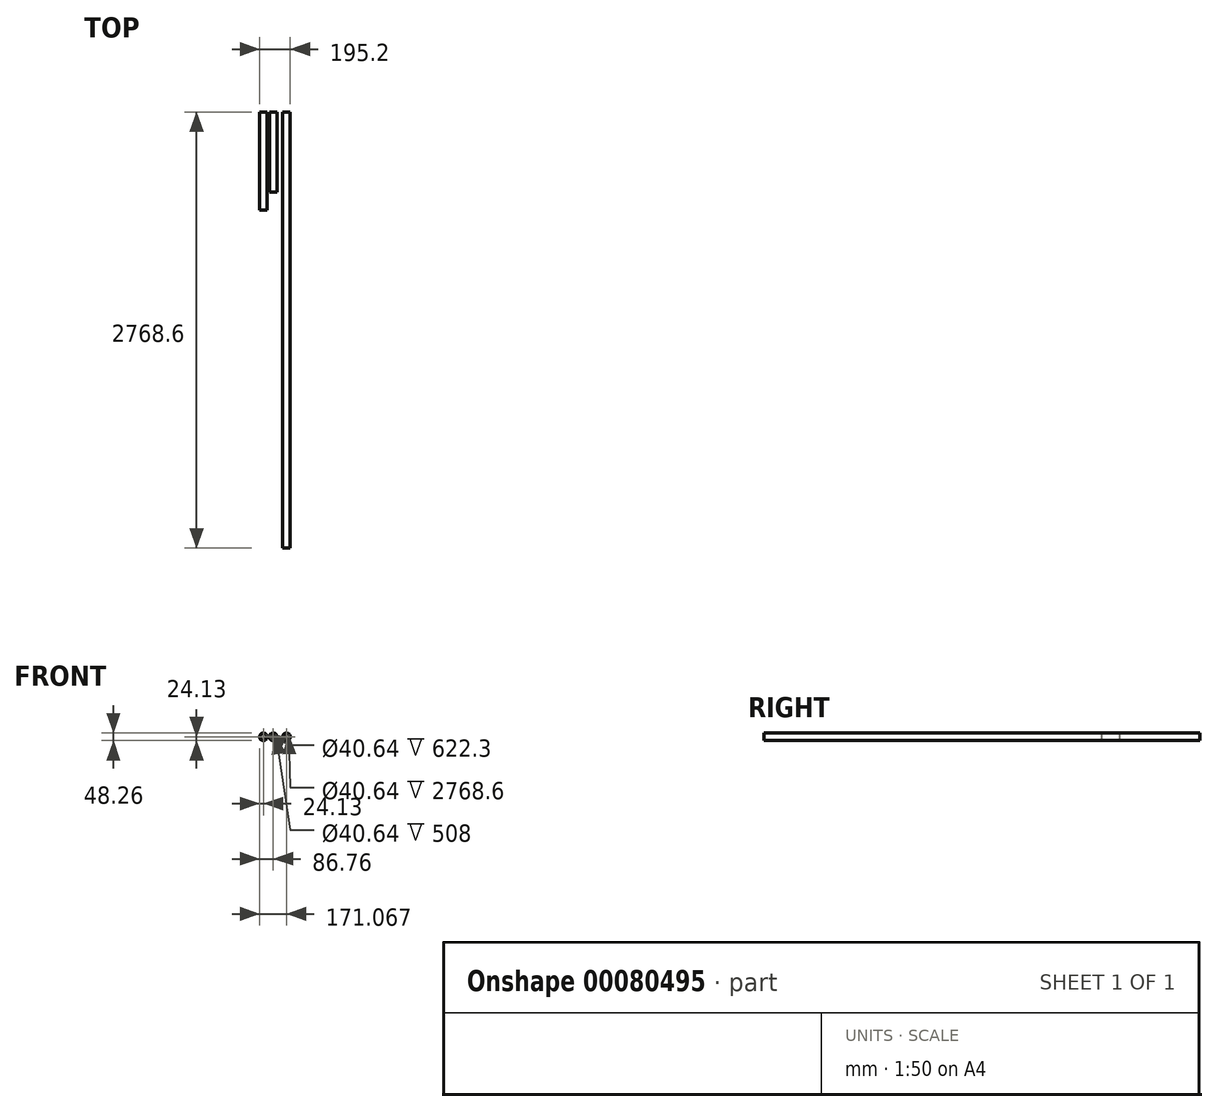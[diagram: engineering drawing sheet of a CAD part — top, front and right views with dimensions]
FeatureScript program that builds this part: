
annotation { "Feature Type Name" : "Feature", "Feature Type Description" : "" }
export const myFeature = defineFeature(function(context is Context, id is Id, definition is map)
    precondition{}
    {
        {
            var Q0;
            Q0=qCreatedBy(makeId("Front.planeOp"),FACE);
            var sketch = newSketch(context, id + "F0", { "sketchPlane" : qUnion([Q0])});
            skCircle(sketch, "E0", {"center": v(0, 0) * mm, "radius": 20.32 * mm});
            skCircle(sketch, "E1", {"center": v(0, 0) * mm, "radius": 24.13 * mm});
            skSolve(sketch);
        }
        {
            var Q0;
            Q0 = qSketchRegion(id + "F0", true);
            extrude(context, id + "F1", {"entities" : qUnion([Q0]), "depth" : 508 * mm});
        }
        {
            var Q0;
            Q0=qCreatedBy(makeId("Front.planeOp"),FACE);
            var sketch = newSketch(context, id + "F2", { "sketchPlane" : qUnion([Q0])});
            skCircle(sketch, "E2", {"center": v(84.3, 0) * mm, "radius": 20.32 * mm});
            skCircle(sketch, "E3", {"center": v(84.3, 0) * mm, "radius": 24.13 * mm});
            skSolve(sketch);
        }
        {
            var Q0;
            Q0 = qSketchRegion(id + "F2", true);
            extrude(context, id + "F3", {"entities" : qUnion([Q0]), "depth" : 2768.6 * mm});
        }
        {
            var Q0;
            Q0=qCreatedBy(makeId("Front.planeOp"),FACE);
            var sketch = newSketch(context, id + "F4", { "sketchPlane" : qUnion([Q0])});
            skCircle(sketch, "E4", {"center": v(-62.63, 0) * mm, "radius": 20.32 * mm});
            skCircle(sketch, "E5", {"center": v(-62.63, 0) * mm, "radius": 24.13 * mm});
            skSolve(sketch);
        }
        {
            var Q0;
            Q0 = qSketchRegion(id + "F4", true);
            extrude(context, id + "F5", {"entities" : qUnion([Q0]), "depth" : 622.3 * mm});
        }
    });
